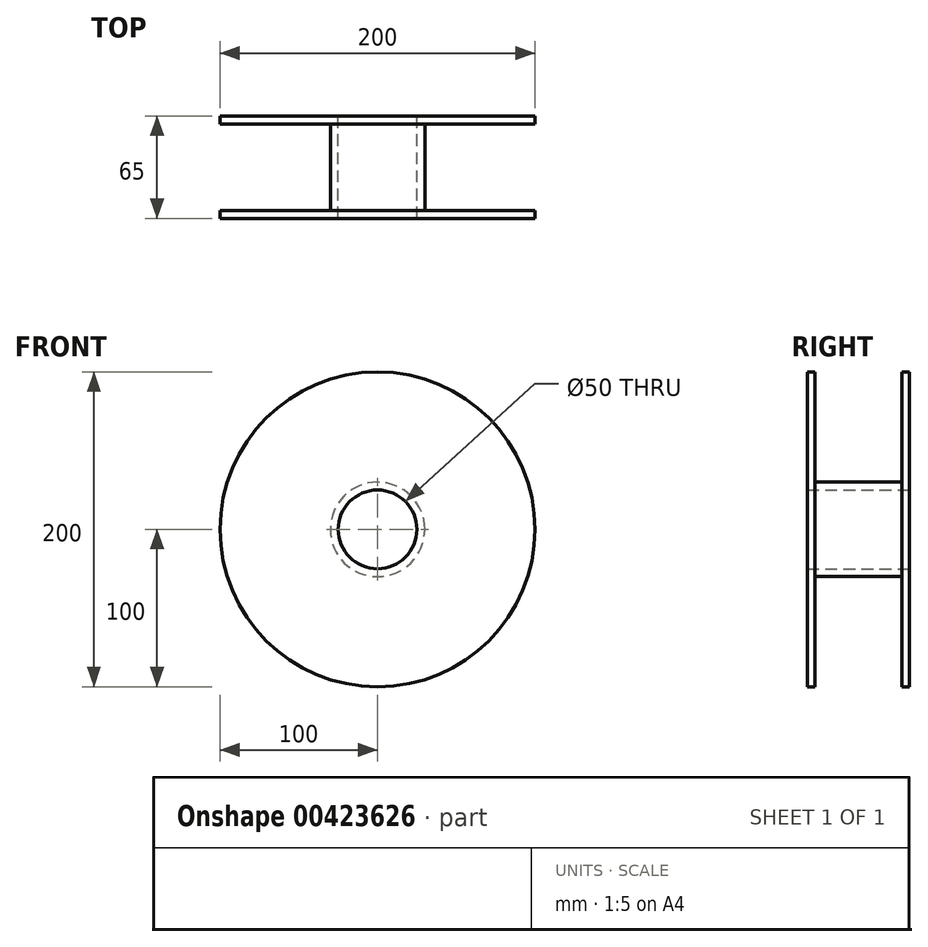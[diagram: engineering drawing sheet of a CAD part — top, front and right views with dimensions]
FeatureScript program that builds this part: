
annotation { "Feature Type Name" : "Feature", "Feature Type Description" : "" }
export const myFeature = defineFeature(function(context is Context, id is Id, definition is map)
    precondition{}
    {
        {
            var Q0;
            Q0=qCreatedBy(makeId("Front.planeOp"),FACE);
            var sketch = newSketch(context, id + "F0", { "sketchPlane" : qUnion([Q0])});
            skCircle(sketch, "E0", {"center": v(0, 0) * mm, "radius": 100 * mm});
            skCircle(sketch, "E1", {"center": v(0, 0) * mm, "radius": 25 * mm});
            skSolve(sketch);
        }
        {
            var Q0;
            Q0=makeQuery(id+"F0.imprint","IMPRINT",FACE,{"disambiguationData":[TD([[makeQuery(id+"F0.imprint","IMPRINT",EDGE,{"derivedFrom":sQuery(id+"F0.wireOp",EDGE,"E0")}),1.0]])]});
            extrude(context, id + "F1", {"entities" : qUnion([Q0]), "endBound" : BoundingType.SYMMETRIC, "depth" : 65 * mm});
        }
        {
            var Q0;
            Q0=makeQuery(id+"F1.opExtrude","SWEPT_FACE",FACE,{"disambiguationData":[OSD([sQuery(id+"F0.wireOp",EDGE,"E0")])]});
            shell(context, id + "F2", {"entities" : qUnion([Q0]), "thickness" : 5 * mm});
        }
    });
